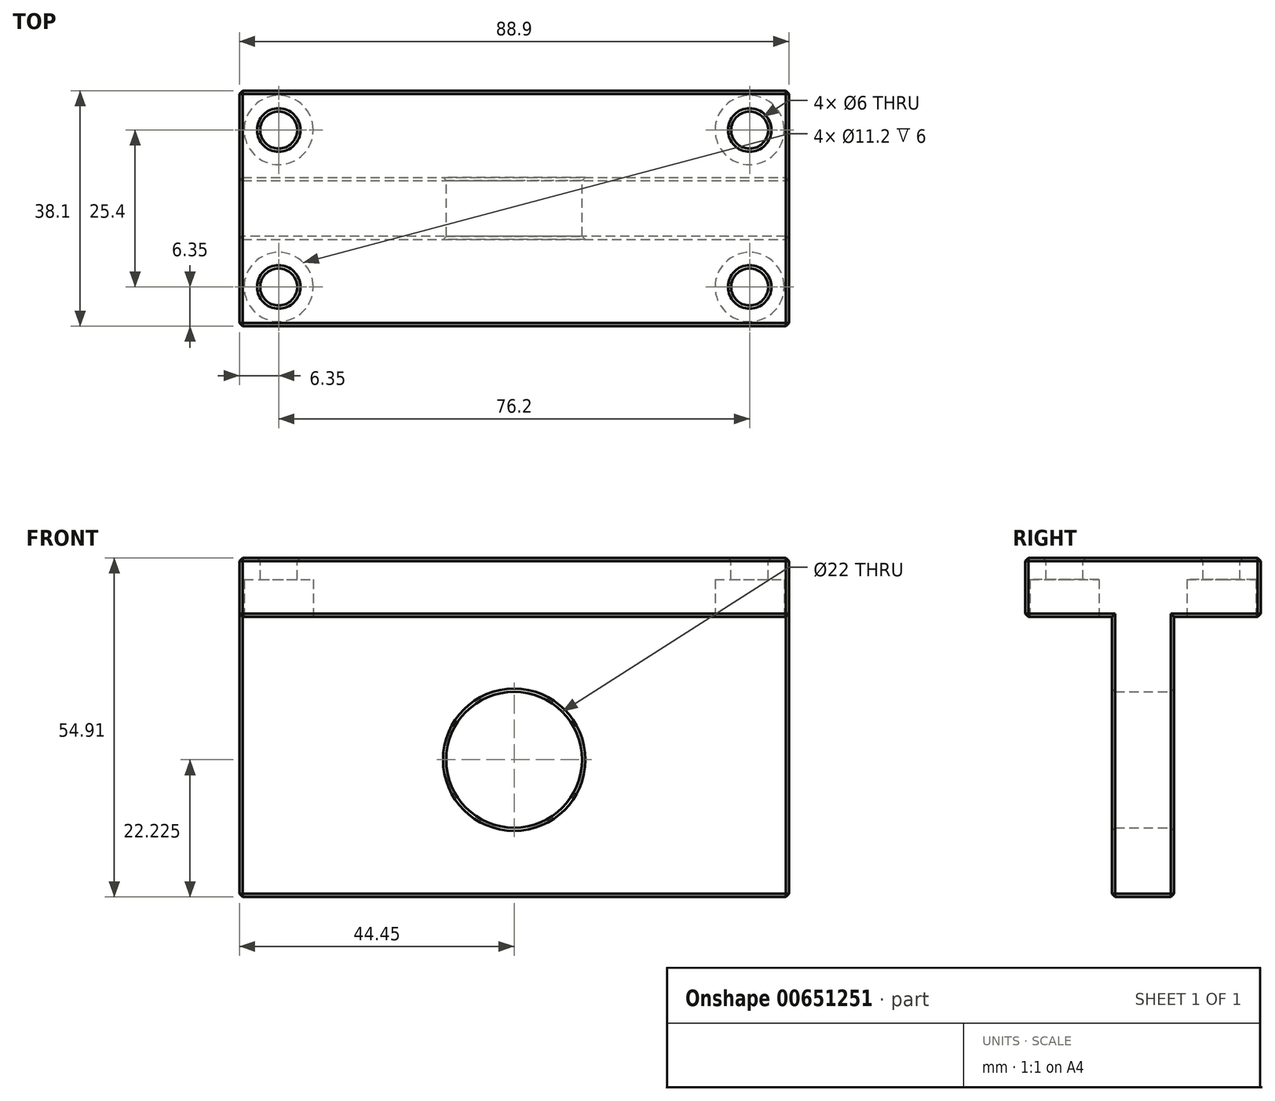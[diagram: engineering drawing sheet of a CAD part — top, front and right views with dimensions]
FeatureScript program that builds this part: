
annotation { "Feature Type Name" : "Feature", "Feature Type Description" : "" }
export const myFeature = defineFeature(function(context is Context, id is Id, definition is map)
    precondition{}
    {
        {
            var Q0;
            Q0=qCreatedBy(makeId("Front.planeOp"),FACE);
            var sketch = newSketch(context, id + "F0", { "sketchPlane" : qUnion([Q0])});
            skLineSegment(sketch, "E0.top", {"start": v(44.45, 16.34) * mm, "end": v(-44.45, 16.34) * mm});
            skLineSegment(sketch, "E0.left", {"start": v(44.45, -16.34) * mm, "end": v(44.45, 16.34) * mm});
            skLineSegment(sketch, "E0.right", {"start": v(-44.45, -16.34) * mm, "end": v(-44.45, 16.34) * mm});
            skPoint(sketch, "E0.middle", {"position": v(0, 0) * mm});
            skCircle(sketch, "E1", {"center": v(0, -16.34) * mm, "radius": 11 * mm});
            skLineSegment(sketch, "E2.top", {"start": v(-44.45, -38.57) * mm, "end": v(44.45, -38.57) * mm});
            skLineSegment(sketch, "E2.left", {"start": v(-44.45, -16.34) * mm, "end": v(-44.45, -38.57) * mm});
            skLineSegment(sketch, "E2.right", {"start": v(44.45, -16.34) * mm, "end": v(44.45, -38.57) * mm});
            skSolve(sketch);
        }
        {
            var Q0;
            Q0=makeQuery(id+"F0.imprint","IMPRINT",FACE,{"disambiguationData":[TD([[makeQuery(id+"F0.imprint","IMPRINT",EDGE,{"derivedFrom":sQuery(id+"F0.wireOp",EDGE,"E0.top")}),1.0]])]});
            extrude(context, id + "F1", {"entities" : qUnion([Q0]), "depth" : 10 * mm, "offsetDistance" : 25.4 * mm});
        }
        {
            var Q0;
            Q0=makeQuery(id+"F1.opExtrude","CAP_FACE",FACE,{"disambiguationData":[OSD([sQuery(id+"F0.wireOp",EDGE,"E0.top"),sQuery(id+"F0.wireOp",EDGE,"E0.left"),sQuery(id+"F0.wireOp",EDGE,"E0.right"),sQuery(id+"F0.wireOp",EDGE,"E1"),sQuery(id+"F0.wireOp",EDGE,"E2.top"),sQuery(id+"F0.wireOp",EDGE,"E2.left"),sQuery(id+"F0.wireOp",EDGE,"E2.right")])],"isStart":false});
            var sketch = newSketch(context, id + "F2", { "sketchPlane" : qUnion([Q0])});
            skCircle(sketch, "E3", {"center": v(0, -16.34) * mm, "radius": 21 * mm});
            skLineSegment(sketch, "E4.bottom", {"start": v(44.45, 16.34) * mm, "end": v(-44.45, 16.34) * mm});
            skLineSegment(sketch, "E4.top", {"start": v(44.45, 6.82) * mm, "end": v(-44.45, 6.82) * mm});
            skLineSegment(sketch, "E4.left", {"start": v(44.45, 16.34) * mm, "end": v(44.45, 6.82) * mm});
            skLineSegment(sketch, "E4.right", {"start": v(-44.45, 16.34) * mm, "end": v(-44.45, 6.82) * mm});
            skSolve(sketch);
        }
        {
            var Q0;
            Q0=makeQuery(id+"F2.imprint","IMPRINT",FACE,{"disambiguationData":[TD([[makeQuery(id+"F2.imprint","IMPRINT",EDGE,{"derivedFrom":sQuery(id+"F2.wireOp",EDGE,"E4.bottom")}),1.0]])]});
            extrude(context, id + "F3", {"entities" : qUnion([Q0]), "operationType" : NewBodyOperationType.ADD, "depth" : 14.05 * mm, "offsetDistance" : 25.4 * mm});
        }
        {
            var Q0;
            Q0=makeQuery(id+"F1.opExtrude","CAP_FACE",FACE,{"disambiguationData":[OSD([sQuery(id+"F0.wireOp",EDGE,"E0.top"),sQuery(id+"F0.wireOp",EDGE,"E0.left"),sQuery(id+"F0.wireOp",EDGE,"E0.right"),sQuery(id+"F0.wireOp",EDGE,"E1"),sQuery(id+"F0.wireOp",EDGE,"E2.top"),sQuery(id+"F0.wireOp",EDGE,"E2.left"),sQuery(id+"F0.wireOp",EDGE,"E2.right")])],"isStart":true});
            var sketch = newSketch(context, id + "F4", { "sketchPlane" : qUnion([Q0])});
            skLineSegment(sketch, "E5.bottom", {"start": v(44.45, 16.34) * mm, "end": v(-44.45, 16.34) * mm});
            skLineSegment(sketch, "E5.top", {"start": v(44.45, 6.82) * mm, "end": v(-44.45, 6.82) * mm});
            skLineSegment(sketch, "E5.left", {"start": v(44.45, 16.34) * mm, "end": v(44.45, 6.82) * mm});
            skLineSegment(sketch, "E5.right", {"start": v(-44.45, 16.34) * mm, "end": v(-44.45, 6.82) * mm});
            skSolve(sketch);
        }
        {
            var Q0;
            Q0=makeQuery(id+"F4.imprint","IMPRINT",FACE,{"disambiguationData":[TD([[makeQuery(id+"F4.imprint","IMPRINT",EDGE,{"derivedFrom":sQuery(id+"F4.wireOp",EDGE,"E5.bottom")}),-1.0]])]});
            extrude(context, id + "F5", {"entities" : qUnion([Q0]), "operationType" : NewBodyOperationType.ADD, "depth" : 14.05 * mm, "offsetDistance" : 25.4 * mm});
        }
        {
            var Q0;
            Q0=makeQuery(id+"F5.boolean.opBoolean","MERGE",FACE,{"derivedFrom":[makeQuery(id+"F3.boolean.opBoolean","MERGE",FACE,{"derivedFrom":[makeQuery(id+"F1.opExtrude","SWEPT_FACE",FACE,{"disambiguationData":[OSD([sQuery(id+"F0.wireOp",EDGE,"E0.top")])]}),makeQuery(id+"F3.opExtrude","SWEPT_FACE",FACE,{"disambiguationData":[OSD([sQuery(id+"F2.wireOp",EDGE,"E4.bottom")])]})]}),makeQuery(id+"F5.opExtrude","SWEPT_FACE",FACE,{"disambiguationData":[OSD([sQuery(id+"F4.wireOp",EDGE,"E5.bottom")])]})]});
            var sketch = newSketch(context, id + "F6", { "sketchPlane" : qUnion([Q0])});
            skPoint(sketch, "E6.middle", {"position": v(0, -5) * mm});
            skCircle(sketch, "E7", {"center": v(-38.1, 7.7) * mm, "radius": 3 * mm});
            skCircle(sketch, "E8", {"center": v(-38.1, -17.7) * mm, "radius": 3 * mm});
            skCircle(sketch, "E9", {"center": v(38.1, 7.7) * mm, "radius": 3 * mm});
            skCircle(sketch, "E10", {"center": v(38.1, -17.7) * mm, "radius": 3 * mm});
            skSolve(sketch);
        }
        {
            var Q0;
            Q0=makeQuery(id+"F6.imprint","IMPRINT",FACE,{"disambiguationData":[TD([[makeQuery(id+"F6.imprint","IMPRINT",EDGE,{"derivedFrom":sQuery(id+"F6.wireOp",EDGE,"E7")}),1.0]])]});
            var Q1;
            Q1=makeQuery(id+"F6.imprint","IMPRINT",FACE,{"disambiguationData":[TD([[makeQuery(id+"F6.imprint","IMPRINT",EDGE,{"derivedFrom":sQuery(id+"F6.wireOp",EDGE,"E10")}),1.0]])]});
            var Q2;
            Q2=makeQuery(id+"F6.imprint","IMPRINT",FACE,{"disambiguationData":[TD([[makeQuery(id+"F6.imprint","IMPRINT",EDGE,{"derivedFrom":sQuery(id+"F6.wireOp",EDGE,"E9")}),1.0]])]});
            var Q3;
            Q3=makeQuery(id+"F6.imprint","IMPRINT",FACE,{"disambiguationData":[TD([[makeQuery(id+"F6.imprint","IMPRINT",EDGE,{"derivedFrom":sQuery(id+"F6.wireOp",EDGE,"E8")}),1.0]])]});
            extrude(context, id + "F7", {"entities" : qUnion([Q0, Q1, Q2, Q3]), "operationType" : NewBodyOperationType.REMOVE, "endBound" : BoundingType.THROUGH_ALL, "oppositeDirection" : true, "depth" : 9.52 * mm, "offsetDistance" : 25.4 * mm});
        }
        {
            var Q0;
            Q0=makeQuery(id+"F3.opExtrude","SWEPT_FACE",FACE,{"disambiguationData":[OSD([sQuery(id+"F2.wireOp",EDGE,"E4.top")])]});
            var sketch = newSketch(context, id + "F8", { "sketchPlane" : qUnion([Q0])});
            skCircle(sketch, "E11", {"center": v(-38.1, 17.7) * mm, "radius": 5.6 * mm});
            skCircle(sketch, "E12", {"center": v(38.1, 17.7) * mm, "radius": 5.6 * mm});
            skSolve(sketch);
        }
        {
            var Q0;
            Q0=makeQuery(id+"F8.imprint","IMPRINT",FACE,{"disambiguationData":[TD([[makeQuery(id+"F8.imprint","IMPRINT",EDGE,{"derivedFrom":sQuery(id+"F8.wireOp",EDGE,"E11")}),1.0]])]});
            var Q1;
            Q1=makeQuery(id+"F8.imprint","IMPRINT",FACE,{"disambiguationData":[TD([[makeQuery(id+"F8.imprint","IMPRINT",EDGE,{"derivedFrom":sQuery(id+"F8.wireOp",EDGE,"E12")}),1.0]])]});
            extrude(context, id + "F9", {"entities" : qUnion([Q0, Q1]), "operationType" : NewBodyOperationType.REMOVE, "oppositeDirection" : true, "depth" : 6 * mm, "offsetDistance" : 25.4 * mm});
        }
        {
            var Q0;
            Q0=makeQuery(id+"F5.opExtrude","SWEPT_FACE",FACE,{"disambiguationData":[OSD([sQuery(id+"F4.wireOp",EDGE,"E5.top")])]});
            var sketch = newSketch(context, id + "F10", { "sketchPlane" : qUnion([Q0])});
            skCircle(sketch, "E13", {"center": v(-38.1, -7.7) * mm, "radius": 5.6 * mm});
            skCircle(sketch, "E14", {"center": v(38.1, -7.7) * mm, "radius": 5.6 * mm});
            skSolve(sketch);
        }
        {
            var Q0;
            Q0=makeQuery(id+"F10.imprint","IMPRINT",FACE,{"disambiguationData":[TD([[makeQuery(id+"F10.imprint","IMPRINT",EDGE,{"derivedFrom":sQuery(id+"F10.wireOp",EDGE,"E13")}),1.0]])]});
            var Q1;
            Q1=makeQuery(id+"F10.imprint","IMPRINT",FACE,{"disambiguationData":[TD([[makeQuery(id+"F10.imprint","IMPRINT",EDGE,{"derivedFrom":sQuery(id+"F10.wireOp",EDGE,"E14")}),1.0]])]});
            extrude(context, id + "F11", {"entities" : qUnion([Q0, Q1]), "operationType" : NewBodyOperationType.REMOVE, "oppositeDirection" : true, "depth" : 6 * mm, "offsetDistance" : 25.4 * mm});
        }
        {
            var Q0;
            Q0=makeQuery(id+"F11.boolean.opBoolean","COPY",EDGE,{"derivedFrom":makeQuery(id+"F11.opExtrude","CAP_EDGE",EDGE,{"disambiguationData":[OSD([sQuery(id+"F10.wireOp",EDGE,"E13")])],"isStart":true})});
            var Q1;
            Q1=makeQuery(id+"F11.boolean.opBoolean","COPY",EDGE,{"derivedFrom":makeQuery(id+"F11.opExtrude","CAP_EDGE",EDGE,{"disambiguationData":[OSD([sQuery(id+"F10.wireOp",EDGE,"E14")])],"isStart":true})});
            var Q2;
            Q2=makeQuery(id+"F9.boolean.opBoolean","COPY",EDGE,{"derivedFrom":makeQuery(id+"F9.opExtrude","CAP_EDGE",EDGE,{"disambiguationData":[OSD([sQuery(id+"F8.wireOp",EDGE,"E12")])],"isStart":true})});
            var Q3;
            Q3=makeQuery(id+"F9.boolean.opBoolean","COPY",EDGE,{"derivedFrom":makeQuery(id+"F9.opExtrude","CAP_EDGE",EDGE,{"disambiguationData":[OSD([sQuery(id+"F8.wireOp",EDGE,"E11")])],"isStart":true})});
            var Q4;
            Q4=makeQuery(id+"F1.opExtrude","CAP_EDGE",EDGE,{"disambiguationData":[OSD([sQuery(id+"F0.wireOp",EDGE,"E1")])],"isStart":false});
            var Q5;
            Q5=makeQuery(id+"F1.opExtrude","CAP_EDGE",EDGE,{"disambiguationData":[OSD([sQuery(id+"F0.wireOp",EDGE,"E1")])],"isStart":true});
            chamfer(context, id + "F12", {"entities" : qUnion([Q0, Q1, Q2, Q3, Q4, Q5]), "width" : 0.5 * mm, "tangentPropagation" : true});
        }
        {
            var Q0;
            Q0=makeQuery(id+"F1.opExtrude","SWEPT_FACE",FACE,{"disambiguationData":[OSD([sQuery(id+"F0.wireOp",EDGE,"E2.top")])]});
            var Q1;
            Q1=makeQuery(id+"F5.boolean.opBoolean","MERGE",FACE,{"derivedFrom":[makeQuery(id+"F3.boolean.opBoolean","MERGE",FACE,{"derivedFrom":[makeQuery(id+"F1.opExtrude","SWEPT_FACE",FACE,{"disambiguationData":[OSD([sQuery(id+"F0.wireOp",EDGE,"E0.right"),sQuery(id+"F0.wireOp",EDGE,"E2.left")])]}),makeQuery(id+"F3.opExtrude","SWEPT_FACE",FACE,{"disambiguationData":[OSD([sQuery(id+"F2.wireOp",EDGE,"E4.right")])]})]}),makeQuery(id+"F5.opExtrude","SWEPT_FACE",FACE,{"disambiguationData":[OSD([sQuery(id+"F4.wireOp",EDGE,"E5.left")])]})]});
            var Q2;
            Q2=makeQuery(id+"F5.boolean.opBoolean","MERGE",FACE,{"derivedFrom":[makeQuery(id+"F3.boolean.opBoolean","MERGE",FACE,{"derivedFrom":[makeQuery(id+"F1.opExtrude","SWEPT_FACE",FACE,{"disambiguationData":[OSD([sQuery(id+"F0.wireOp",EDGE,"E0.left"),sQuery(id+"F0.wireOp",EDGE,"E2.right")])]}),makeQuery(id+"F3.opExtrude","SWEPT_FACE",FACE,{"disambiguationData":[OSD([sQuery(id+"F2.wireOp",EDGE,"E4.left")])]})]}),makeQuery(id+"F5.opExtrude","SWEPT_FACE",FACE,{"disambiguationData":[OSD([sQuery(id+"F4.wireOp",EDGE,"E5.right")])]})]});
            var Q3;
            Q3=makeQuery(id+"F3.opExtrude","CAP_FACE",FACE,{"disambiguationData":[OSD([sQuery(id+"F2.wireOp",EDGE,"E4.bottom"),sQuery(id+"F2.wireOp",EDGE,"E4.top"),sQuery(id+"F2.wireOp",EDGE,"E4.left"),sQuery(id+"F2.wireOp",EDGE,"E4.right")])],"isStart":false});
            var Q4;
            Q4=makeQuery(id+"F5.opExtrude","CAP_FACE",FACE,{"disambiguationData":[OSD([sQuery(id+"F4.wireOp",EDGE,"E5.bottom"),sQuery(id+"F4.wireOp",EDGE,"E5.top"),sQuery(id+"F4.wireOp",EDGE,"E5.left"),sQuery(id+"F4.wireOp",EDGE,"E5.right")])],"isStart":false});
            var Q5;
            Q5=makeQuery(id+"F5.boolean.opBoolean","MERGE",FACE,{"derivedFrom":[makeQuery(id+"F3.boolean.opBoolean","MERGE",FACE,{"derivedFrom":[makeQuery(id+"F1.opExtrude","SWEPT_FACE",FACE,{"disambiguationData":[OSD([sQuery(id+"F0.wireOp",EDGE,"E0.top")])]}),makeQuery(id+"F3.opExtrude","SWEPT_FACE",FACE,{"disambiguationData":[OSD([sQuery(id+"F2.wireOp",EDGE,"E4.bottom")])]})]}),makeQuery(id+"F5.opExtrude","SWEPT_FACE",FACE,{"disambiguationData":[OSD([sQuery(id+"F4.wireOp",EDGE,"E5.bottom")])]})]});
            chamfer(context, id + "F13", {"entities" : qUnion([Q0, Q1, Q2, Q3, Q4, Q5]), "width" : 0.5 * mm, "tangentPropagation" : true});
        }
    });
